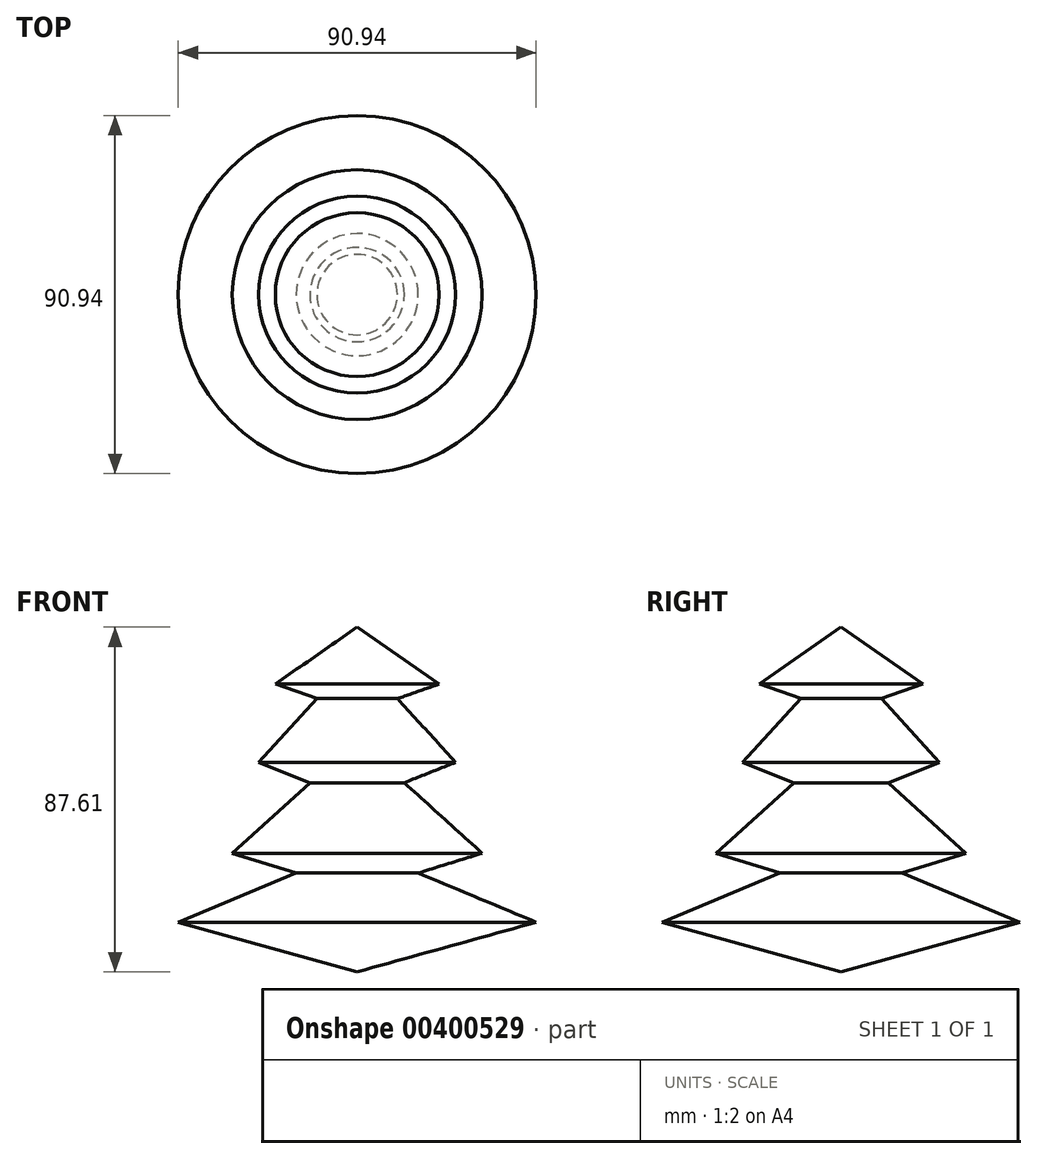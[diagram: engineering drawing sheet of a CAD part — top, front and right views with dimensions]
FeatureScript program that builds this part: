
annotation { "Feature Type Name" : "Feature", "Feature Type Description" : "" }
export const myFeature = defineFeature(function(context is Context, id is Id, definition is map)
    precondition{}
    {
        {
            var Q0;
            Q0=qCreatedBy(makeId("Front.planeOp"),FACE);
            var sketch = newSketch(context, id + "F0", { "sketchPlane" : qUnion([Q0])});
            skLineSegment(sketch, "E0", {"start": v(-20.8, 24.66) * mm, "end": v(-20.8, -62.95) * mm});
            skLineSegment(sketch, "E1", {"start": v(-20.8, 24.66) * mm, "end": v(0, 10.18) * mm});
            skLineSegment(sketch, "E2", {"start": v(0, 10.18) * mm, "end": v(-10.57, 6.46) * mm});
            skLineSegment(sketch, "E3", {"start": v(-10.57, 6.46) * mm, "end": v(4.23, -9.7) * mm});
            skLineSegment(sketch, "E4", {"start": v(4.23, -9.7) * mm, "end": v(-8.81, -14.88) * mm});
            skLineSegment(sketch, "E5", {"start": v(-8.81, -14.88) * mm, "end": v(10.93, -32.8) * mm});
            skLineSegment(sketch, "E6", {"start": v(10.93, -32.8) * mm, "end": v(-5.29, -37.83) * mm});
            skLineSegment(sketch, "E7", {"start": v(-5.29, -37.83) * mm, "end": v(24.67, -50.33) * mm});
            skLineSegment(sketch, "E8", {"start": v(24.67, -50.33) * mm, "end": v(-20.8, -62.95) * mm});
            skSolve(sketch);
        }
        {
            var Q0;
            Q0=makeQuery(id+"F0.imprint","IMPRINT",FACE,{"disambiguationData":[TD([[makeQuery(id+"F0.imprint","IMPRINT",EDGE,{"derivedFrom":sQuery(id+"F0.wireOp",EDGE,"E0")}),1.0]])]});
            var Q1;
            Q1=sQuery(id+"F0.wireOp",EDGE,"E0");
            revolve(context, id + "F1", {"entities" : qUnion([Q0]), "axis" : qUnion([Q1]), "revolveType" : RevolveType.FULL});
        }
    });
